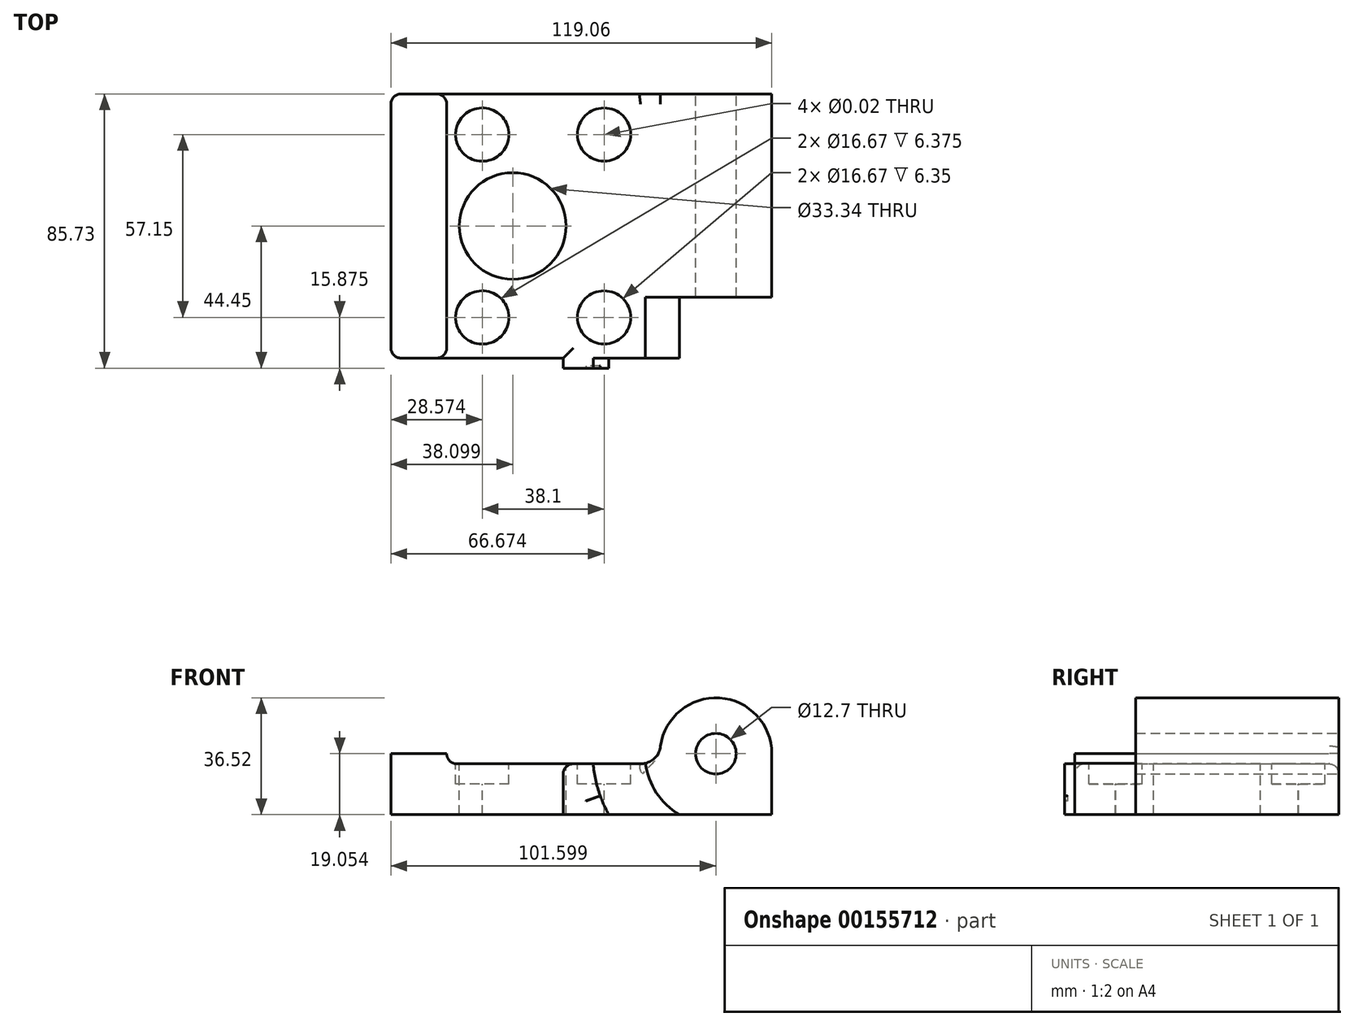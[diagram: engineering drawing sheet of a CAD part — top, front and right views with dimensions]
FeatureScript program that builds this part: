
annotation { "Feature Type Name" : "Feature", "Feature Type Description" : "" }
export const myFeature = defineFeature(function(context is Context, id is Id, definition is map)
    precondition{}
    {
        {
            var Q0;
            Q0=qCreatedBy(makeId("Front.planeOp"),FACE);
            var sketch = newSketch(context, id + "F0", { "sketchPlane" : qUnion([Q0])});
            skLineSegment(sketch, "E0.top", {"start": v(59.53, -18.26) * mm, "end": v(-59.53, -18.26) * mm});
            skLineSegment(sketch, "E0.left", {"start": v(59.53, 0.8) * mm, "end": v(59.53, -18.26) * mm});
            skLineSegment(sketch, "E0.right", {"start": v(-59.53, 0.8) * mm, "end": v(-59.53, -18.26) * mm});
            skLineSegment(sketch, "E1", {"start": v(-59.53, 0.8) * mm, "end": v(-42.07, 0.8) * mm});
            skLineSegment(sketch, "E2", {"start": v(-42.07, 0.8) * mm, "end": v(-42.07, 0.8) * mm});
            skLineSegment(sketch, "E3", {"start": v(-38.9, -2.38) * mm, "end": v(24.6, -2.38) * mm});
            skArc(sketch, "E4", {"start": v(59.53, 0.8) * mm, "mid": v(42.07, 18.26) * mm, "end": v(24.6, 0.8) * mm});
            skPoint(sketch, "E5", {"position": v(42.07, 18.26) * mm});
            skLineSegment(sketch, "E6", {"start": v(0, -18.26) * mm, "end": v(0, 18.26) * mm, "construction": true});
            skCircle(sketch, "E7", {"center": v(42.07, 0.8) * mm, "radius": 6.35 * mm});
            skArc(sketch, "E8.filletArc", {"start": v(-42.07, 0.8) * mm, "mid": v(-41.14, -1.45) * mm, "end": v(-38.9, -2.38) * mm});
            skLineSegment(sketch, "E9", {"start": v(24.6, 0.8) * mm, "end": v(24.6, -2.38) * mm});
            skSolve(sketch);
        }
        {
            var Q0;
            Q0 = qSketchRegion(id + "F0", true);
            extrude(context, id + "F1", {"entities" : qUnion([Q0]), "endBound" : BoundingType.SYMMETRIC, "depth" : 82.55 * mm});
        }
        {
            var Q0;
            Q0=makeQuery(id+"F1.opExtrude","CAP_FACE",FACE,{"disambiguationData":[OSD([sQuery(id+"F0.wireOp",EDGE,"E0.top"),sQuery(id+"F0.wireOp",EDGE,"E0.left"),sQuery(id+"F0.wireOp",EDGE,"E0.right"),sQuery(id+"F0.wireOp",EDGE,"E1"),sQuery(id+"F0.wireOp",EDGE,"E3"),sQuery(id+"F0.wireOp",EDGE,"E4"),sQuery(id+"F0.wireOp",EDGE,"E7"),sQuery(id+"F0.wireOp",EDGE,"E8.filletArc"),sQuery(id+"F0.wireOp",EDGE,"E9")])],"isStart":false});
            var sketch = newSketch(context, id + "F2", { "sketchPlane" : qUnion([Q0])});
            skLineSegment(sketch, "E10", {"start": v(-5.65, -2.38) * mm, "end": v(-5.65, -18.26) * mm});
            skArc(sketch, "E11", {"start": v(3.72, -2.38) * mm, "mid": v(5.3, -10.59) * mm, "end": v(8.63, -18.26) * mm});
            skLineSegment(sketch, "E12", {"start": v(3.72, -2.38) * mm, "end": v(-5.65, -2.38) * mm});
            skLineSegment(sketch, "E13", {"start": v(-5.65, -18.26) * mm, "end": v(8.63, -18.26) * mm});
            skSolve(sketch);
        }
        {
            var Q0;
            Q0 = qSketchRegion(id + "F2", true);
            extrude(context, id + "F3", {"entities" : qUnion([Q0]), "operationType" : NewBodyOperationType.ADD, "depth" : 3.17 * mm});
        }
        {
            var Q0;
            {var subQ0=sQuery(id+"F0.wireOp",EDGE,"E4");var subQ1=sQuery(id+"F0.wireOp",EDGE,"E3");var subQ2=sQuery(id+"F0.wireOp",EDGE,"E0.left");var subQ3=sQuery(id+"F0.wireOp",EDGE,"E9");var subQ4=sQuery(id+"F0.wireOp",EDGE,"E0.top");var subQ5=sQuery(id+"F0.wireOp",EDGE,"E7");Q0=makeQuery(id+"F3.boolean.opBoolean","SPLIT",FACE,{"disambiguationData":[TD([makeQuery(id+"F1.opExtrude","SWEPT_FACE",FACE,{"disambiguationData":[OSD([subQ2])]})])],"derivedFrom":makeQuery(id+"F1.opExtrude","CAP_FACE",FACE,{"disambiguationData":[OSD([subQ4,subQ2,sQuery(id+"F0.wireOp",EDGE,"E0.right"),sQuery(id+"F0.wireOp",EDGE,"E1"),subQ1,subQ0,subQ5,sQuery(id+"F0.wireOp",EDGE,"E8.filletArc"),subQ3])],"isStart":false})});}
            var sketch = newSketch(context, id + "F4", { "sketchPlane" : qUnion([Q0])});
            skArc(sketch, "E14", {"start": v(20.07, -2.38) * mm, "mid": v(23.56, -11.5) * mm, "end": v(30.62, -18.26) * mm});
            skLineSegment(sketch, "E15", {"start": v(20.07, -2.38) * mm, "end": v(24.6, -2.38) * mm});
            skLineSegment(sketch, "E16", {"start": v(30.62, -18.26) * mm, "end": v(59.53, -18.26) * mm});
            skLineSegment(sketch, "E17.0", {"start": v(59.53, 0.8) * mm, "end": v(59.53, -18.26) * mm});
            skArc(sketch, "E18.0", {"start": v(59.53, 0.8) * mm, "mid": v(42.07, 18.26) * mm, "end": v(24.6, 0.8) * mm});
            skLineSegment(sketch, "E19.0", {"start": v(24.6, 0.8) * mm, "end": v(24.6, -2.38) * mm});
            skSolve(sketch);
        }
        {
            var Q0;
            Q0 = qSketchRegion(id + "F4", true);
            extrude(context, id + "F5", {"entities" : qUnion([Q0]), "operationType" : NewBodyOperationType.REMOVE, "oppositeDirection" : true, "depth" : 19.05 * mm});
        }
        {
            var Q0;
            Q0=makeQuery(id+"F1.opExtrude","SWEPT_FACE",FACE,{"disambiguationData":[OSD([sQuery(id+"F0.wireOp",EDGE,"E1")])]});
            var sketch = newSketch(context, id + "F6", { "sketchPlane" : qUnion([Q0])});
            skPoint(sketch, "E20", {"position": v(-21.43, 0) * mm});
            skPoint(sketch, "E21", {"position": v(-30.96, 28.58) * mm});
            skPoint(sketch, "E22", {"position": v(7.14, 28.58) * mm});
            skPoint(sketch, "E23", {"position": v(7.14, -28.58) * mm});
            skPoint(sketch, "E24", {"position": v(-30.96, -28.58) * mm});
            skSolve(sketch);
        }
        {
            var Q0;
            Q0=sQuery(id+"F6.wireOp",VERTEX,"E20");
            var Q1;
            Q1=makeQuery(id+"F1.opExtrude","SWEPT_BODY",BODY,{"disambiguationData":[OSD([sQuery(id+"F0.wireOp",EDGE,"E0.top"),sQuery(id+"F0.wireOp",EDGE,"E0.left"),sQuery(id+"F0.wireOp",EDGE,"E0.right"),sQuery(id+"F0.wireOp",EDGE,"E1"),sQuery(id+"F0.wireOp",EDGE,"E3"),sQuery(id+"F0.wireOp",EDGE,"E4"),sQuery(id+"F0.wireOp",EDGE,"E7"),sQuery(id+"F0.wireOp",EDGE,"E8.filletArc"),sQuery(id+"F0.wireOp",EDGE,"E9")])]});
            hole(context, id + "F7", {"style" : HoleStyle.SIMPLE, "endStyle" : HoleEndStyle.THROUGH, "holeDiameter" : 33.34 * mm, "startFromSketch" : true, "locations" : qUnion([Q0]), "scope" : qUnion([Q1]), "isTappedThrough" : true});
        }
        {
            var Q0;
            Q0=sQuery(id+"F6.wireOp",VERTEX,"E21");
            var Q1;
            Q1=sQuery(id+"F6.wireOp",VERTEX,"E22");
            var Q2;
            Q2=sQuery(id+"F6.wireOp",VERTEX,"E23");
            var Q3;
            Q3=sQuery(id+"F6.wireOp",VERTEX,"E24");
            var Q4;
            Q4=makeQuery(id+"F1.opExtrude","SWEPT_BODY",BODY,{"disambiguationData":[OSD([sQuery(id+"F0.wireOp",EDGE,"E0.top"),sQuery(id+"F0.wireOp",EDGE,"E0.left"),sQuery(id+"F0.wireOp",EDGE,"E0.right"),sQuery(id+"F0.wireOp",EDGE,"E1"),sQuery(id+"F0.wireOp",EDGE,"E3"),sQuery(id+"F0.wireOp",EDGE,"E4"),sQuery(id+"F0.wireOp",EDGE,"E7"),sQuery(id+"F0.wireOp",EDGE,"E8.filletArc"),sQuery(id+"F0.wireOp",EDGE,"E9")])]});
            hole(context, id + "F8", {"style" : HoleStyle.C_BORE, "endStyle" : HoleEndStyle.THROUGH, "standardTappedOrClearance" : lookupTablePath({ "standard" : "ANSI", "size" : "15/32 (0.47)", "type" : "Drilled" }), "standardBlindInLast" : lookupTablePath({ "standard" : "ANSI", "size" : "15/32", "type" : "Drilled" }), "holeDiameter" : 15 / 812.8 * mm, "cBoreDiameter" : 16.67 * mm, "cBoreDepth" : 6.35 * mm, "locations" : qUnion([Q0, Q1, Q2, Q3]), "scope" : qUnion([Q4]), "isTappedThrough" : true});
        }
        {
            var Q0;
            {var subQ0=sQuery(id+"F0.wireOp",EDGE,"E3");var subQ1=sQuery(id+"F0.wireOp",EDGE,"E8.filletArc");Q0=makeQuery(id+"F3.boolean.opBoolean","SPLIT",EDGE,{"disambiguationData":[TD([makeQuery(id+"F1.opExtrude","SWEPT_FACE",FACE,{"disambiguationData":[OSD([subQ1])]})])],"derivedFrom":makeQuery(id+"F1.opExtrude","CAP_EDGE",EDGE,{"disambiguationData":[OSD([subQ0])],"isStart":false})});}
            var Q1;
            Q1=makeQuery(id+"F1.opExtrude","CAP_EDGE",EDGE,{"disambiguationData":[OSD([sQuery(id+"F0.wireOp",EDGE,"E0.right")])],"isStart":false});
            var Q2;
            Q2=makeQuery(id+"F1.opExtrude","CAP_EDGE",EDGE,{"disambiguationData":[OSD([sQuery(id+"F0.wireOp",EDGE,"E3")])],"isStart":true});
            var Q3;
            Q3=makeQuery(id+"F1.opExtrude","CAP_EDGE",EDGE,{"disambiguationData":[OSD([sQuery(id+"F0.wireOp",EDGE,"E0.right")])],"isStart":true});
            var Q4;
            Q4=makeQuery(id+"F3.opExtrude","SWEPT_EDGE",EDGE,{"disambiguationData":[OSD([sQuery(id+"F0.wireOp",EDGE,"E3"),sQuery(id+"F2.wireOp",EDGE,"E10"),sQuery(id+"F2.wireOp",EDGE,"E12")])]});
            var Q5;
            Q5=makeQuery(id+"F7.hole-0.boolean.opBoolean","INTERSECT",EDGE,{"derivedFrom":[makeQuery(id+"F3.boolean.opBoolean","MERGE",FACE,{"derivedFrom":[makeQuery(id+"F1.opExtrude","SWEPT_FACE",FACE,{"disambiguationData":[OSD([sQuery(id+"F0.wireOp",EDGE,"E3")])]}),makeQuery(id+"F3.opExtrude","SWEPT_FACE",FACE,{"disambiguationData":[OSD([sQuery(id+"F2.wireOp",EDGE,"E12")])]})]}),makeQuery(id+"F7.hole-0.opRevolve","SWEPT_FACE",FACE,{"disambiguationData":[OSD([sQuery(id+"F7.hole-0.sketch.wireOp",EDGE,"core_line_2")])]})]});
            fillet(context, id + "F9", {"entities" : qUnion([Q0, Q1, Q2, Q3, Q4, Q5]), "radius" : 3.17 * mm, "tangentPropagation" : true, "allowEdgeOverflow" : false});
        }
        {
            var Q0;
            Q0=makeQuery(id+"F1.opExtrude","SWEPT_EDGE",EDGE,{"disambiguationData":[OSD([sQuery(id+"F0.wireOp",EDGE,"E3"),sQuery(id+"F0.wireOp",EDGE,"E9")])]});
            fillet(context, id + "F10", {"entities" : qUnion([Q0]), "radius" : 6.35 * mm, "tangentPropagation" : true, "allowEdgeOverflow" : false});
        }
        {
            var Q0;
            Q0=makeQuery(id+"F3.opExtrude","CAP_FACE",FACE,{"disambiguationData":[OSD([sQuery(id+"F2.wireOp",EDGE,"E10"),sQuery(id+"F2.wireOp",EDGE,"E11"),sQuery(id+"F2.wireOp",EDGE,"E12"),sQuery(id+"F2.wireOp",EDGE,"E13")])],"isStart":false});
            var sketch = newSketch(context, id + "F11", { "sketchPlane" : qUnion([Q0])});
            skLineSegment(sketch, "E25", {"start": v(42.07, 0.8) * mm, "end": v(3.59, 0.8) * mm, "construction": true});
            skLineSegment(sketch, "E26", {"start": v(42.07, 0.8) * mm, "end": v(5.9, -12.37) * mm, "construction": true});
            skLineSegment(sketch, "E27.bottom", {"start": v(5.93, -12.41) * mm, "end": v(1.45, -14.04) * mm});
            skLineSegment(sketch, "E27.top", {"start": v(5.9, -12.32) * mm, "end": v(1.42, -13.95) * mm});
            skLineSegment(sketch, "E27.left", {"start": v(5.93, -12.41) * mm, "end": v(5.9, -12.32) * mm});
            skLineSegment(sketch, "E27.right", {"start": v(1.45, -14.04) * mm, "end": v(1.42, -13.95) * mm});
            skSolve(sketch);
        }
        {
            var Q0;
            Q0 = qSketchRegion(id + "F11", true);
            extrude(context, id + "F12", {"entities" : qUnion([Q0]), "operationType" : NewBodyOperationType.REMOVE, "oppositeDirection" : true, "depth" : 0.8 * mm});
        }
    });
